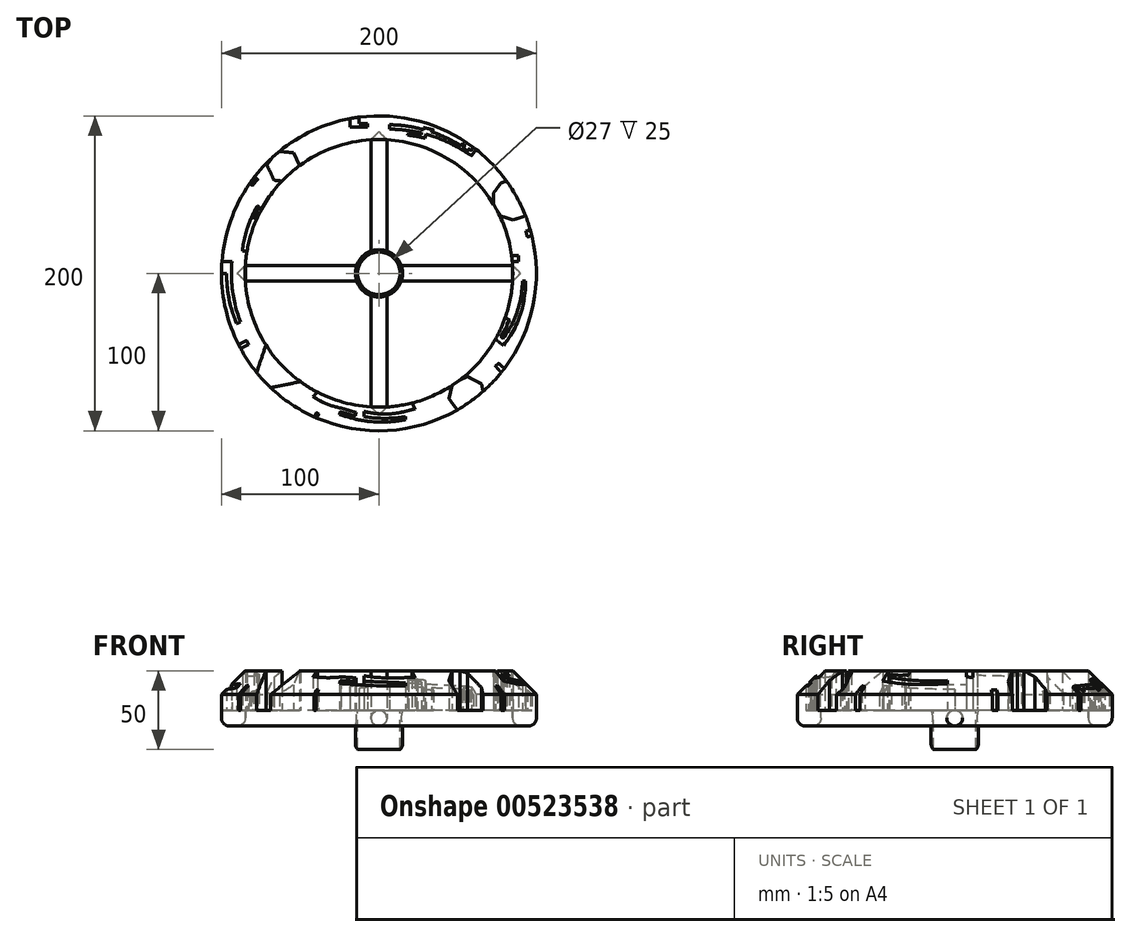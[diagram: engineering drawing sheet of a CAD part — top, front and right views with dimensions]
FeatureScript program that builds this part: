
annotation { "Feature Type Name" : "Feature", "Feature Type Description" : "" }
export const myFeature = defineFeature(function(context is Context, id is Id, definition is map)
    precondition{}
    {
        {
            var Q0;
            Q0=qCreatedBy(makeId("Top.planeOp"),FACE);
            var sketch = newSketch(context, id + "F0", { "sketchPlane" : qUnion([Q0])});
            skArc(sketch, "E0", {"start": v(-5, 14.14) * mm, "mid": v(-10.6, 10.6) * mm, "end": v(-14.14, 5) * mm});
            skCircle(sketch, "E1", {"center": v(0, 0) * mm, "radius": 13.5 * mm});
            skLineSegment(sketch, "E2.left", {"start": v(-5, 84.85) * mm, "end": v(-5, 14.14) * mm});
            skLineSegment(sketch, "E2.right", {"start": v(5, 84.85) * mm, "end": v(5, 14.14) * mm});
            skLineSegment(sketch, "E3.bottom", {"start": v(84.85, 5) * mm, "end": v(14.14, 5) * mm});
            skLineSegment(sketch, "E3.top", {"start": v(84.85, -5) * mm, "end": v(14.14, -5) * mm});
            skArc(sketch, "E4.trimOffspring", {"start": v(14.14, 5) * mm, "mid": v(10.6, 10.6) * mm, "end": v(5, 14.14) * mm});
            skLineSegment(sketch, "E5.MirrorCS", {"start": v(-84.85, 5) * mm, "end": v(-14.14, 5) * mm});
            skLineSegment(sketch, "E6.MirrorCS", {"start": v(-84.85, -5) * mm, "end": v(-14.14, -5) * mm});
            skLineSegment(sketch, "E7.MirrorCS", {"start": v(5, -84.85) * mm, "end": v(5, -14.14) * mm});
            skLineSegment(sketch, "E8.MirrorCS", {"start": v(-5, -84.85) * mm, "end": v(-5, -14.14) * mm});
            skArc(sketch, "E9.trimOffspring", {"start": v(-14.14, -5) * mm, "mid": v(-10.6, -10.6) * mm, "end": v(-5, -14.14) * mm});
            skArc(sketch, "E10.trimOffspring", {"start": v(5, -14.14) * mm, "mid": v(10.6, -10.6) * mm, "end": v(14.14, -5) * mm});
            skCircle(sketch, "E11", {"center": v(0, 0) * mm, "radius": 100 * mm});
            skArc(sketch, "E12", {"start": v(-5, 84.85) * mm, "mid": v(-60.1, 60.1) * mm, "end": v(-84.85, 5) * mm});
            skArc(sketch, "E13.trimOffspring", {"start": v(84.85, 5) * mm, "mid": v(60.1, 60.1) * mm, "end": v(5, 84.85) * mm});
            skArc(sketch, "E14.trimOffspring", {"start": v(5, -84.85) * mm, "mid": v(60.1, -60.1) * mm, "end": v(84.85, -5) * mm});
            skArc(sketch, "E15.trimOffspring", {"start": v(-84.85, -5) * mm, "mid": v(-60.1, -60.1) * mm, "end": v(-5, -84.85) * mm});
            skLineSegment(sketch, "E16", {"start": v(-5, -84.85) * mm, "end": v(5, -84.85) * mm});
            skLineSegment(sketch, "E17", {"start": v(-84.85, 5) * mm, "end": v(-84.85, -5) * mm});
            skLineSegment(sketch, "E18", {"start": v(-5, 84.85) * mm, "end": v(5, 84.85) * mm});
            skLineSegment(sketch, "E19", {"start": v(84.85, 5) * mm, "end": v(84.85, -5) * mm});
            skArc(sketch, "E20", {"start": v(-14.14, 5) * mm, "mid": v(-15, 0) * mm, "end": v(-14.14, -5) * mm});
            skArc(sketch, "E21.MirrorCS", {"start": v(14.14, 5) * mm, "mid": v(15, 0) * mm, "end": v(14.14, -5) * mm});
            skArc(sketch, "E22", {"start": v(5, 14.14) * mm, "mid": v(0, 15) * mm, "end": v(-5, 14.14) * mm});
            skArc(sketch, "E23.MirrorCS", {"start": v(5, -14.14) * mm, "mid": v(0, -15) * mm, "end": v(-5, -14.14) * mm});
            skLineSegment(sketch, "E24", {"start": v(-100, 0) * mm, "end": v(-96.68, 0) * mm});
            skArc(sketch, "E25", {"start": v(-96.68, 0) * mm, "mid": v(-95.19, -16.22) * mm, "end": v(-90.38, -31.79) * mm});
            skLineSegment(sketch, "E26", {"start": v(-90.38, -31.79) * mm, "end": v(-87.85, -30.9) * mm});
            skArc(sketch, "E27", {"start": v(-93.32, 7.4) * mm, "mid": v(-92.88, -12.07) * mm, "end": v(-87.85, -30.9) * mm});
            skLineSegment(sketch, "E28", {"start": v(-93.32, 7.4) * mm, "end": v(-99.73, 7.4) * mm});
            skLineSegment(sketch, "E29", {"start": v(-83.79, 14.3) * mm, "end": v(-86.74, 14.3) * mm});
            skArc(sketch, "E30", {"start": v(-77.16, 42.9) * mm, "mid": v(-83.42, 29.09) * mm, "end": v(-86.74, 14.3) * mm});
            skLineSegment(sketch, "E31", {"start": v(-77.16, 42.9) * mm, "end": v(-76.17, 42.27) * mm});
            skArc(sketch, "E32", {"start": v(-76.17, 42.27) * mm, "mid": v(-77.82, 38.73) * mm, "end": v(-79.37, 35.15) * mm});
            skCircle(sketch, "E33.cCircle", {"center": v(-67.46, -62.6) * mm, "radius": 9.56 * mm, "construction": true});
            skLineSegment(sketch, "E33.0", {"start": v(-71.24, -43.87) * mm, "end": v(-49.35, -68.7) * mm});
            skLineSegment(sketch, "E33.1", {"start": v(-49.35, -68.7) * mm, "end": v(-81.8, -75.24) * mm});
            skLineSegment(sketch, "E33.2", {"start": v(-81.8, -75.24) * mm, "end": v(-71.24, -43.87) * mm});
            skPoint(sketch, "E33.0.midPoint", {"position": v(-60.3, -56.29) * mm});
            skLineSegment(sketch, "E34", {"start": v(-39.13, -75.46) * mm, "end": v(-41.87, -78.2) * mm});
            skArc(sketch, "E35", {"start": v(-41.87, -78.2) * mm, "mid": v(-33.42, -82.83) * mm, "end": v(-24.16, -85.55) * mm});
            skLineSegment(sketch, "E36", {"start": v(-24.16, -85.55) * mm, "end": v(-14.47, -88.4) * mm});
            skLineSegment(sketch, "E37", {"start": v(-14.47, -88.4) * mm, "end": v(-15.12, -90.62) * mm});
            skLineSegment(sketch, "E38", {"start": v(-15.12, -90.62) * mm, "end": v(-24.5, -87.86) * mm});
            skLineSegment(sketch, "E39", {"start": v(-24.5, -87.86) * mm, "end": v(-25, -89.53) * mm});
            skArc(sketch, "E40", {"start": v(-25, -89.53) * mm, "mid": v(-4.24, -94.25) * mm, "end": v(17.01, -92.9) * mm});
            skLineSegment(sketch, "E41", {"start": v(17.01, -92.9) * mm, "end": v(17.01, -91.03) * mm});
            skArc(sketch, "E42", {"start": v(-9.52, -91.03) * mm, "mid": v(3.75, -92.05) * mm, "end": v(17.01, -91.03) * mm});
            skLineSegment(sketch, "E43", {"start": v(-9.52, -91.03) * mm, "end": v(-9.52, -87.66) * mm});
            skArc(sketch, "E44", {"start": v(-9.52, -87.66) * mm, "mid": v(3.6, -89.35) * mm, "end": v(16.74, -87.66) * mm});
            skLineSegment(sketch, "E45", {"start": v(16.74, -87.66) * mm, "end": v(22.99, -86.02) * mm});
            skLineSegment(sketch, "E46", {"start": v(22.99, -86.02) * mm, "end": v(20.92, -82.39) * mm});
            skCircle(sketch, "E47.cCircle", {"center": v(55.83, -77.24) * mm, "radius": 10.55 * mm, "construction": true});
            skLineSegment(sketch, "E47.0", {"start": v(46.85, -69.73) * mm, "end": v(56.1, -65.54) * mm});
            skLineSegment(sketch, "E47.1", {"start": v(56.1, -65.54) * mm, "end": v(65.15, -70.16) * mm});
            skLineSegment(sketch, "E47.2", {"start": v(65.15, -70.16) * mm, "end": v(67.18, -80.12) * mm});
            skLineSegment(sketch, "E47.3", {"start": v(67.18, -80.12) * mm, "end": v(60.66, -87.9) * mm});
            skLineSegment(sketch, "E47.4", {"start": v(60.66, -87.9) * mm, "end": v(50.5, -87.67) * mm});
            skLineSegment(sketch, "E47.5", {"start": v(50.5, -87.67) * mm, "end": v(44.36, -79.58) * mm});
            skLineSegment(sketch, "E47.6", {"start": v(44.36, -79.58) * mm, "end": v(46.85, -69.73) * mm});
            skPoint(sketch, "E47.0.midPoint", {"position": v(51.48, -67.64) * mm});
            skLineSegment(sketch, "E48", {"start": v(77.65, -63) * mm, "end": v(73.98, -58.89) * mm});
            skLineSegment(sketch, "E49", {"start": v(73.98, -58.89) * mm, "end": v(75.97, -57.12) * mm});
            skLineSegment(sketch, "E50", {"start": v(75.97, -57.12) * mm, "end": v(79.75, -60.34) * mm});
            skLineSegment(sketch, "E51", {"start": v(73.99, -41.84) * mm, "end": v(78.99, -45.84) * mm});
            skArc(sketch, "E52", {"start": v(78.99, -45.84) * mm, "mid": v(89.74, -26.58) * mm, "end": v(93.05, -4.77) * mm});
            skLineSegment(sketch, "E53", {"start": v(93.05, -4.77) * mm, "end": v(91.07, -4.77) * mm});
            skArc(sketch, "E54", {"start": v(78.9, -41.47) * mm, "mid": v(87.9, -24.09) * mm, "end": v(91.07, -4.77) * mm});
            skLineSegment(sketch, "E55", {"start": v(78.9, -41.47) * mm, "end": v(77.59, -40.15) * mm});
            skLineSegment(sketch, "E56", {"start": v(77.59, -40.15) * mm, "end": v(81.36, -33.65) * mm});
            skLineSegment(sketch, "E57", {"start": v(81.36, -33.65) * mm, "end": v(81.36, -32.04) * mm});
            skLineSegment(sketch, "E58", {"start": v(81.36, -32.04) * mm, "end": v(82.77, -29.5) * mm});
            skLineSegment(sketch, "E59", {"start": v(82.77, -29.5) * mm, "end": v(80.23, -28.08) * mm});
            skLineSegment(sketch, "E60", {"start": v(84.67, 7.5) * mm, "end": v(88.52, 7.5) * mm});
            skLineSegment(sketch, "E61", {"start": v(88.52, 7.5) * mm, "end": v(88.52, 11.47) * mm});
            skLineSegment(sketch, "E62", {"start": v(88.52, 11.47) * mm, "end": v(84.22, 11.47) * mm});
            skCircle(sketch, "E63.cCircle", {"center": v(85.2, 46.94) * mm, "radius": 12.38 * mm, "construction": true});
            skLineSegment(sketch, "E63.0", {"start": v(77.55, 36.4) * mm, "end": v(72.82, 42.9) * mm});
            skLineSegment(sketch, "E63.1", {"start": v(72.82, 42.9) * mm, "end": v(72.81, 50.95) * mm});
            skLineSegment(sketch, "E63.2", {"start": v(72.81, 50.95) * mm, "end": v(77.54, 57.46) * mm});
            skLineSegment(sketch, "E63.3", {"start": v(77.54, 57.46) * mm, "end": v(85.18, 59.95) * mm});
            skLineSegment(sketch, "E63.4", {"start": v(85.18, 59.95) * mm, "end": v(92.84, 57.47) * mm});
            skLineSegment(sketch, "E63.5", {"start": v(92.84, 57.47) * mm, "end": v(97.57, 50.97) * mm});
            skLineSegment(sketch, "E63.6", {"start": v(97.57, 50.97) * mm, "end": v(97.58, 42.92) * mm});
            skLineSegment(sketch, "E63.7", {"start": v(97.58, 42.92) * mm, "end": v(92.85, 36.41) * mm});
            skLineSegment(sketch, "E63.8", {"start": v(92.85, 36.41) * mm, "end": v(85.2, 33.92) * mm});
            skLineSegment(sketch, "E63.9", {"start": v(85.2, 33.92) * mm, "end": v(77.55, 36.4) * mm});
            skPoint(sketch, "E63.0.midPoint", {"position": v(75.19, 39.65) * mm});
            skLineSegment(sketch, "E64", {"start": v(96.13, 27.54) * mm, "end": v(93.26, 26.73) * mm});
            skLineSegment(sketch, "E65", {"start": v(93.26, 26.73) * mm, "end": v(94.27, 23.14) * mm});
            skLineSegment(sketch, "E66", {"start": v(94.27, 23.14) * mm, "end": v(97.1, 23.93) * mm});
            skLineSegment(sketch, "E67", {"start": v(-39.8, -91.74) * mm, "end": v(-38.3, -89.3) * mm});
            skLineSegment(sketch, "E68", {"start": v(-38.3, -89.3) * mm, "end": v(-39.65, -88.48) * mm});
            skLineSegment(sketch, "E69", {"start": v(-39.65, -88.48) * mm, "end": v(-41.26, -91.1) * mm});
            skLineSegment(sketch, "E70", {"start": v(-89.13, -45.34) * mm, "end": v(-84.06, -42.72) * mm});
            skLineSegment(sketch, "E71", {"start": v(-84.06, -42.72) * mm, "end": v(-82.82, -45.13) * mm});
            skLineSegment(sketch, "E72", {"start": v(-82.82, -45.13) * mm, "end": v(-87.87, -47.74) * mm});
            skCircle(sketch, "E73.cCircle", {"center": v(-60.49, 67.89) * mm, "radius": 9.28 * mm, "construction": true});
            skLineSegment(sketch, "E73.0", {"start": v(-71.15, 68.96) * mm, "end": v(-64.89, 77.65) * mm});
            skLineSegment(sketch, "E73.1", {"start": v(-64.89, 77.65) * mm, "end": v(-54.23, 76.58) * mm});
            skLineSegment(sketch, "E73.2", {"start": v(-54.23, 76.58) * mm, "end": v(-49.82, 66.81) * mm});
            skLineSegment(sketch, "E73.3", {"start": v(-49.82, 66.81) * mm, "end": v(-56.08, 58.12) * mm});
            skLineSegment(sketch, "E73.4", {"start": v(-56.08, 58.12) * mm, "end": v(-66.74, 59.19) * mm});
            skLineSegment(sketch, "E73.5", {"start": v(-66.74, 59.19) * mm, "end": v(-71.15, 68.96) * mm});
            skPoint(sketch, "E73.0.midPoint", {"position": v(-68.02, 73.3) * mm});
            skLineSegment(sketch, "E74", {"start": v(-79.37, 35.15) * mm, "end": v(-77.84, 34.16) * mm});
            skLineSegment(sketch, "E75", {"start": v(-82.17, 56.99) * mm, "end": v(-80.14, 55.86) * mm});
            skLineSegment(sketch, "E76", {"start": v(-80.14, 55.86) * mm, "end": v(-78.62, 57.77) * mm});
            skLineSegment(sketch, "E77", {"start": v(-78.62, 57.77) * mm, "end": v(-77, 59.62) * mm});
            skLineSegment(sketch, "E78", {"start": v(-77, 59.62) * mm, "end": v(-77.79, 60.31) * mm});
            skLineSegment(sketch, "E79", {"start": v(-77.79, 60.31) * mm, "end": v(-79.63, 58.22) * mm});
            skLineSegment(sketch, "E80", {"start": v(-79.63, 58.22) * mm, "end": v(-81.06, 58.56) * mm});
            skLineSegment(sketch, "E81", {"start": v(61.81, 78.6) * mm, "end": v(58.84, 74.8) * mm});
            skLineSegment(sketch, "E82", {"start": v(58.84, 74.8) * mm, "end": v(51.74, 79.02) * mm});
            skArc(sketch, "E83", {"start": v(51.74, 79.02) * mm, "mid": v(41.1, 84.42) * mm, "end": v(29.84, 88.35) * mm});
            skLineSegment(sketch, "E84", {"start": v(6.7, 91.56) * mm, "end": v(6.7, 94.36) * mm});
            skArc(sketch, "E85", {"start": v(28.45, 91.11) * mm, "mid": v(17.7, 93.58) * mm, "end": v(6.7, 94.36) * mm});
            skLineSegment(sketch, "E86", {"start": v(28.45, 91.11) * mm, "end": v(28.45, 92.57) * mm});
            skLineSegment(sketch, "E87", {"start": v(28.45, 92.57) * mm, "end": v(34.73, 91.11) * mm});
            skLineSegment(sketch, "E88", {"start": v(34.73, 91.11) * mm, "end": v(33.38, 89.88) * mm});
            skArc(sketch, "E89", {"start": v(52, 81.13) * mm, "mid": v(42.94, 86.04) * mm, "end": v(33.38, 89.88) * mm});
            skLineSegment(sketch, "E90", {"start": v(52, 81.13) * mm, "end": v(53, 82.36) * mm});
            skLineSegment(sketch, "E91", {"start": v(53, 82.36) * mm, "end": v(54.52, 81.13) * mm});
            skLineSegment(sketch, "E92", {"start": v(54.52, 81.13) * mm, "end": v(53.54, 79.94) * mm});
            skLineSegment(sketch, "E93", {"start": v(53.54, 79.94) * mm, "end": v(56.18, 77.78) * mm});
            skLineSegment(sketch, "E94", {"start": v(56.18, 77.78) * mm, "end": v(57.2, 79.04) * mm});
            skLineSegment(sketch, "E95", {"start": v(57.2, 79.04) * mm, "end": v(58.37, 78.08) * mm});
            skLineSegment(sketch, "E96", {"start": v(58.37, 78.08) * mm, "end": v(59.97, 80.02) * mm});
            skLineSegment(sketch, "E97", {"start": v(24.01, 86.97) * mm, "end": v(29.33, 85.87) * mm});
            skLineSegment(sketch, "E98", {"start": v(29.33, 85.87) * mm, "end": v(29.84, 88.35) * mm});
            skArc(sketch, "E99.trimOffspring", {"start": v(24.56, 89.64) * mm, "mid": v(15.68, 91.05) * mm, "end": v(6.7, 91.56) * mm});
            skLineSegment(sketch, "E100", {"start": v(24.01, 86.97) * mm, "end": v(18.03, 87.87) * mm});
            skLineSegment(sketch, "E101", {"start": v(18.03, 87.87) * mm, "end": v(18.88, 88.9) * mm});
            skLineSegment(sketch, "E102", {"start": v(27.09, 88.05) * mm, "end": v(27.09, 89.47) * mm});
            skLineSegment(sketch, "E103", {"start": v(27.09, 89.47) * mm, "end": v(24.56, 89.64) * mm});
            skArc(sketch, "E104", {"start": v(27.09, 88.05) * mm, "mid": v(23, 88.6) * mm, "end": v(18.88, 88.9) * mm});
            skLineSegment(sketch, "E105", {"start": v(-12.67, 99.2) * mm, "end": v(-12.67, 95.26) * mm});
            skLineSegment(sketch, "E106", {"start": v(-12.67, 95.26) * mm, "end": v(-7.13, 95.26) * mm});
            skLineSegment(sketch, "E107", {"start": v(-7.13, 95.26) * mm, "end": v(-7.13, 93) * mm});
            skLineSegment(sketch, "E108", {"start": v(-7.13, 93) * mm, "end": v(-13.92, 93) * mm});
            skLineSegment(sketch, "E109", {"start": v(-13.92, 93) * mm, "end": v(-18.45, 93) * mm});
            skLineSegment(sketch, "E110", {"start": v(-18.45, 93) * mm, "end": v(-18.45, 98.28) * mm});
            skArc(sketch, "E111", {"start": v(-20.15, 86.4) * mm, "mid": v(-34.73, 82.8) * mm, "end": v(-47.5, 74.9) * mm});
            skLineSegment(sketch, "E112", {"start": v(-20.15, 86.4) * mm, "end": v(-20.15, 88.63) * mm});
            skLineSegment(sketch, "E113", {"start": v(-47.5, 74.9) * mm, "end": v(-47.5, 79.2) * mm});
            skArc(sketch, "E114", {"start": v(-20.15, 88.63) * mm, "mid": v(-34.22, 85.34) * mm, "end": v(-47.3, 79.2) * mm});
            skSolve(sketch);
        }
        {
            var Q0;
            Q0=qCreatedBy(makeId("Top.planeOp"),FACE);
            var sketch = newSketch(context, id + "F1", { "sketchPlane" : qUnion([Q0])});
            skCircle(sketch, "E115", {"center": v(0, 0) * mm, "radius": 13.5 * mm});
            skCircle(sketch, "E116", {"center": v(0, 0) * mm, "radius": 15 * mm});
            skCircle(sketch, "E117", {"center": v(0, 0) * mm, "radius": 100 * mm});
            skCircle(sketch, "E118", {"center": v(0, 0) * mm, "radius": 85 * mm});
            skLineSegment(sketch, "E119", {"start": v(-14.14, 5) * mm, "end": v(-84.85, 5) * mm});
            skLineSegment(sketch, "E120", {"start": v(-14.14, -5) * mm, "end": v(-84.85, -5) * mm});
            skLineSegment(sketch, "E121", {"start": v(-5, 84.85) * mm, "end": v(-5, 14.14) * mm});
            skLineSegment(sketch, "E122", {"start": v(5, 14.14) * mm, "end": v(5, 84.85) * mm});
            skLineSegment(sketch, "E123.MirrorCS", {"start": v(14.14, 5) * mm, "end": v(84.85, 5) * mm});
            skLineSegment(sketch, "E124.MirrorCS", {"start": v(14.14, -5) * mm, "end": v(84.85, -5) * mm});
            skLineSegment(sketch, "E125.MirrorCS", {"start": v(-5, -84.85) * mm, "end": v(-5, -14.14) * mm});
            skLineSegment(sketch, "E126.MirrorCS", {"start": v(5, -14.14) * mm, "end": v(5, -84.85) * mm});
            skSolve(sketch);
        }
        {
            var Q0;
            Q0=qCreatedBy(makeId("Top.planeOp"),FACE);
            var sketch = newSketch(context, id + "F2", { "sketchPlane" : qUnion([Q0])});
            skCircle(sketch, "E127", {"center": v(0, 0) * mm, "radius": 13.5 * mm});
            skCircle(sketch, "E128", {"center": v(0, 0) * mm, "radius": 15 * mm});
            skSolve(sketch);
        }
        {
            var Q0;
            {var subQ7=sQuery(id+"F0.wireOp",EDGE,"E34");Q0=makeQuery(id+"F0.imprint","IMPRINT",FACE,{"disambiguationData":[TD([[makeQuery(id+"F0.imprint","IMPRINT",EDGE,{"derivedFrom":subQ7}),-1.0]])]});}
            var Q1;
            {var subQ19=sQuery(id+"F0.wireOp",EDGE,"E17");Q1=makeQuery(id+"F0.imprint","IMPRINT",FACE,{"disambiguationData":[TD([[makeQuery(id+"F0.imprint","IMPRINT",EDGE,{"derivedFrom":subQ19}),-1.0]])]});}
            var Q2;
            {var subQ1=sQuery(id+"F0.wireOp",EDGE,"E18");Q2=makeQuery(id+"F0.imprint","IMPRINT",FACE,{"disambiguationData":[TD([[makeQuery(id+"F0.imprint","IMPRINT",EDGE,{"derivedFrom":subQ1}),1.0]])]});}
            var Q3;
            {var subQ6=sQuery(id+"F0.wireOp",EDGE,"E19");Q3=makeQuery(id+"F0.imprint","IMPRINT",FACE,{"disambiguationData":[TD([[makeQuery(id+"F0.imprint","IMPRINT",EDGE,{"derivedFrom":subQ6}),1.0]])]});}
            extrude(context, id + "F3", {"entities" : qUnion([Q0, Q1, Q2, Q3]), "depth" : 25 * mm, "offsetDistance" : 25 * mm});
        }
        {
            var Q0;
            Q0=makeQuery(id+"F1.imprint","IMPRINT",FACE,{"disambiguationData":[TD([[makeQuery(id+"F1.imprint","IMPRINT",EDGE,{"derivedFrom":sQuery(id+"F1.wireOp",EDGE,"E117")}),1.0]])]});
            var Q1;
            {var subQ0=sQuery(id+"F1.wireOp",EDGE,"E121");Q1=makeQuery(id+"F1.imprint","IMPRINT",FACE,{"disambiguationData":[TD([[makeQuery(id+"F1.imprint","IMPRINT",EDGE,{"derivedFrom":subQ0}),1.0]])]});}
            var Q2;
            {var subQ0=sQuery(id+"F1.wireOp",EDGE,"E119");Q2=makeQuery(id+"F1.imprint","IMPRINT",FACE,{"disambiguationData":[TD([[makeQuery(id+"F1.imprint","IMPRINT",EDGE,{"derivedFrom":subQ0}),1.0]])]});}
            var Q3;
            {var subQ0=sQuery(id+"F1.wireOp",EDGE,"E123.MirrorCS");Q3=makeQuery(id+"F1.imprint","IMPRINT",FACE,{"disambiguationData":[TD([[makeQuery(id+"F1.imprint","IMPRINT",EDGE,{"derivedFrom":subQ0}),-1.0]])]});}
            var Q4;
            {var subQ0=sQuery(id+"F1.wireOp",EDGE,"E125.MirrorCS");Q4=makeQuery(id+"F1.imprint","IMPRINT",FACE,{"disambiguationData":[TD([[makeQuery(id+"F1.imprint","IMPRINT",EDGE,{"derivedFrom":subQ0}),-1.0]])]});}
            var Q5;
            Q5=makeQuery(id+"F1.imprint","IMPRINT",FACE,{"disambiguationData":[TD([[makeQuery(id+"F1.imprint","IMPRINT",EDGE,{"derivedFrom":sQuery(id+"F1.wireOp",EDGE,"E115")}),-1.0]])]});
            extrude(context, id + "F4", {"entities" : qUnion([Q0, Q1, Q2, Q3, Q4, Q5]), "operationType" : NewBodyOperationType.ADD, "oppositeDirection" : true, "depth" : 10 * mm, "offsetDistance" : 25 * mm});
        }
        {
            var Q0;
            Q0=makeQuery(id+"F4.opExtrude","CAP_EDGE",EDGE,{"disambiguationData":[OSD([sQuery(id+"F1.wireOp",EDGE,"E124.MirrorCS")])],"isStart":false});
            var Q1;
            Q1=makeQuery(id+"F4.opExtrude","CAP_EDGE",EDGE,{"disambiguationData":[OSD([sQuery(id+"F1.wireOp",EDGE,"E123.MirrorCS")])],"isStart":false});
            var Q2;
            Q2=makeQuery(id+"F4.opExtrude","CAP_EDGE",EDGE,{"disambiguationData":[OSD([sQuery(id+"F1.wireOp",EDGE,"E124.MirrorCS")])],"isStart":true});
            var Q3;
            Q3=makeQuery(id+"F4.opExtrude","CAP_EDGE",EDGE,{"disambiguationData":[OSD([sQuery(id+"F1.wireOp",EDGE,"E123.MirrorCS")])],"isStart":true});
            var Q4;
            Q4=makeQuery(id+"F4.opExtrude","CAP_EDGE",EDGE,{"disambiguationData":[OSD([sQuery(id+"F1.wireOp",EDGE,"E126.MirrorCS")])],"isStart":false});
            var Q5;
            Q5=makeQuery(id+"F4.opExtrude","CAP_EDGE",EDGE,{"disambiguationData":[OSD([sQuery(id+"F1.wireOp",EDGE,"E125.MirrorCS")])],"isStart":false});
            var Q6;
            Q6=makeQuery(id+"F4.opExtrude","CAP_EDGE",EDGE,{"disambiguationData":[OSD([sQuery(id+"F1.wireOp",EDGE,"E125.MirrorCS")])],"isStart":true});
            var Q7;
            Q7=makeQuery(id+"F4.opExtrude","CAP_EDGE",EDGE,{"disambiguationData":[OSD([sQuery(id+"F1.wireOp",EDGE,"E126.MirrorCS")])],"isStart":true});
            var Q8;
            Q8=makeQuery(id+"F4.opExtrude","CAP_EDGE",EDGE,{"disambiguationData":[OSD([sQuery(id+"F1.wireOp",EDGE,"E120")])],"isStart":true});
            var Q9;
            Q9=makeQuery(id+"F4.opExtrude","CAP_EDGE",EDGE,{"disambiguationData":[OSD([sQuery(id+"F1.wireOp",EDGE,"E120")])],"isStart":false});
            var Q10;
            Q10=makeQuery(id+"F4.opExtrude","CAP_EDGE",EDGE,{"disambiguationData":[OSD([sQuery(id+"F1.wireOp",EDGE,"E119")])],"isStart":false});
            var Q11;
            Q11=makeQuery(id+"F4.opExtrude","CAP_EDGE",EDGE,{"disambiguationData":[OSD([sQuery(id+"F1.wireOp",EDGE,"E119")])],"isStart":true});
            var Q12;
            Q12=makeQuery(id+"F4.opExtrude","CAP_EDGE",EDGE,{"disambiguationData":[OSD([sQuery(id+"F1.wireOp",EDGE,"E122")])],"isStart":false});
            var Q13;
            Q13=makeQuery(id+"F4.opExtrude","CAP_EDGE",EDGE,{"disambiguationData":[OSD([sQuery(id+"F1.wireOp",EDGE,"E122")])],"isStart":true});
            var Q14;
            Q14=makeQuery(id+"F4.opExtrude","CAP_EDGE",EDGE,{"disambiguationData":[OSD([sQuery(id+"F1.wireOp",EDGE,"E121")])],"isStart":true});
            var Q15;
            Q15=makeQuery(id+"F4.opExtrude","CAP_EDGE",EDGE,{"disambiguationData":[OSD([sQuery(id+"F1.wireOp",EDGE,"E121")])],"isStart":false});
            var Q16;
            {var subQ0=sQuery(id+"F1.wireOp",EDGE,"E118");Q16=makeQuery(id+"F4.opExtrude","CAP_EDGE",EDGE,{"disambiguationData":[OSD([subQ0]),TDD([makeQuery(id+"F1.imprint","IMPRINT",EDGE,{"disambiguationData":[TD([[makeQuery(id+"F1.imprint","INTERSECT",VERTEX,{"derivedFrom":[subQ0,sQuery(id+"F1.wireOp",EDGE,"E119")]}),1.0]])],"derivedFrom":subQ0})])],"isStart":false});}
            var Q17;
            {var subQ0=sQuery(id+"F1.wireOp",EDGE,"E118");Q17=makeQuery(id+"F4.opExtrude","CAP_EDGE",EDGE,{"disambiguationData":[OSD([subQ0]),TDD([makeQuery(id+"F1.imprint","IMPRINT",EDGE,{"disambiguationData":[TD([[makeQuery(id+"F1.imprint","INTERSECT",VERTEX,{"derivedFrom":[subQ0,sQuery(id+"F1.wireOp",EDGE,"E122")]}),1.0]])],"derivedFrom":subQ0})])],"isStart":false});}
            var Q18;
            Q18=makeQuery(id+"F4.opExtrude","CAP_EDGE",EDGE,{"disambiguationData":[OSD([sQuery(id+"F1.wireOp",EDGE,"E117")])],"isStart":false});
            var Q19;
            {var subQ0=sQuery(id+"F1.wireOp",EDGE,"E118");Q19=makeQuery(id+"F4.opExtrude","CAP_EDGE",EDGE,{"disambiguationData":[OSD([subQ0]),TDD([makeQuery(id+"F1.imprint","IMPRINT",EDGE,{"disambiguationData":[TD([[makeQuery(id+"F1.imprint","INTERSECT",VERTEX,{"derivedFrom":[subQ0,sQuery(id+"F1.wireOp",EDGE,"E124.MirrorCS")]}),1.0]])],"derivedFrom":subQ0})])],"isStart":false});}
            var Q20;
            {var subQ0=sQuery(id+"F1.wireOp",EDGE,"E118");Q20=makeQuery(id+"F4.opExtrude","CAP_EDGE",EDGE,{"disambiguationData":[OSD([subQ0]),TDD([makeQuery(id+"F1.imprint","IMPRINT",EDGE,{"disambiguationData":[TD([[makeQuery(id+"F1.imprint","INTERSECT",VERTEX,{"derivedFrom":[subQ0,sQuery(id+"F1.wireOp",EDGE,"E120")]}),-1.0]])],"derivedFrom":subQ0})])],"isStart":false});}
            var Q21;
            {var subQ0=sQuery(id+"F1.wireOp",EDGE,"E116");Q21=makeQuery(id+"F4.opExtrude","CAP_EDGE",EDGE,{"disambiguationData":[OSD([subQ0]),TDD([makeQuery(id+"F1.imprint","IMPRINT",EDGE,{"disambiguationData":[TD([[makeQuery(id+"F1.imprint","INTERSECT",VERTEX,{"derivedFrom":[subQ0,sQuery(id+"F1.wireOp",EDGE,"E120")]}),-1.0]])],"derivedFrom":subQ0})])],"isStart":true});}
            var Q22;
            {var subQ0=sQuery(id+"F1.wireOp",EDGE,"E116");Q22=makeQuery(id+"F4.opExtrude","CAP_EDGE",EDGE,{"disambiguationData":[OSD([subQ0]),TDD([makeQuery(id+"F1.imprint","IMPRINT",EDGE,{"disambiguationData":[TD([[makeQuery(id+"F1.imprint","INTERSECT",VERTEX,{"derivedFrom":[subQ0,sQuery(id+"F1.wireOp",EDGE,"E124.MirrorCS")]}),1.0]])],"derivedFrom":subQ0})])],"isStart":true});}
            var Q23;
            {var subQ0=sQuery(id+"F1.wireOp",EDGE,"E116");Q23=makeQuery(id+"F4.opExtrude","CAP_EDGE",EDGE,{"disambiguationData":[OSD([subQ0]),TDD([makeQuery(id+"F1.imprint","IMPRINT",EDGE,{"disambiguationData":[TD([[makeQuery(id+"F1.imprint","INTERSECT",VERTEX,{"derivedFrom":[subQ0,sQuery(id+"F1.wireOp",EDGE,"E122")]}),1.0]])],"derivedFrom":subQ0})])],"isStart":true});}
            var Q24;
            {var subQ0=sQuery(id+"F1.wireOp",EDGE,"E116");Q24=makeQuery(id+"F4.opExtrude","CAP_EDGE",EDGE,{"disambiguationData":[OSD([subQ0]),TDD([makeQuery(id+"F1.imprint","IMPRINT",EDGE,{"disambiguationData":[TD([[makeQuery(id+"F1.imprint","INTERSECT",VERTEX,{"derivedFrom":[subQ0,sQuery(id+"F1.wireOp",EDGE,"E119")]}),1.0]])],"derivedFrom":subQ0})])],"isStart":true});}
            fillet(context, id + "F5", {"entities" : qUnion([Q0, Q1, Q2, Q3, Q4, Q5, Q6, Q7, Q8, Q9, Q10, Q11, Q12, Q13, Q14, Q15, Q16, Q17, Q18, Q19, Q20, Q21, Q22, Q23, Q24]), "radius" : 5 * mm, "tangentPropagation" : true, "allowEdgeOverflow" : false});
        }
        {
            var Q0;
            {var subQ0=sQuery(id+"F0.wireOp",EDGE,"E11");Q0=makeQuery(id+"F3.opExtrude","CAP_EDGE",EDGE,{"disambiguationData":[OSD([subQ0]),TDD([makeQuery(id+"F0.imprint","IMPRINT",EDGE,{"disambiguationData":[TD([[makeQuery(id+"F0.imprint","INTERSECT",VERTEX,{"derivedFrom":[subQ0,sQuery(id+"F0.wireOp",EDGE,"E67")]}),-1.0]])],"derivedFrom":subQ0})])],"isStart":false});}
            var Q1;
            {var subQ0=sQuery(id+"F0.wireOp",EDGE,"E11");Q1=makeQuery(id+"F3.opExtrude","CAP_EDGE",EDGE,{"disambiguationData":[OSD([subQ0]),TDD([makeQuery(id+"F0.imprint","IMPRINT",EDGE,{"disambiguationData":[TD([[makeQuery(id+"F0.imprint","INTERSECT",VERTEX,{"derivedFrom":[subQ0,sQuery(id+"F0.wireOp",EDGE,"E50")]}),-1.0]])],"derivedFrom":subQ0})])],"isStart":false});}
            var Q2;
            {var subQ0=sQuery(id+"F0.wireOp",EDGE,"E11");Q2=makeQuery(id+"F3.opExtrude","CAP_EDGE",EDGE,{"disambiguationData":[OSD([subQ0]),TDD([makeQuery(id+"F0.imprint","IMPRINT",EDGE,{"disambiguationData":[TD([[makeQuery(id+"F0.imprint","INTERSECT",VERTEX,{"derivedFrom":[subQ0,sQuery(id+"F0.wireOp",EDGE,"E81")]}),1.0]])],"derivedFrom":subQ0})])],"isStart":false});}
            var Q3;
            {var subQ0=sQuery(id+"F0.wireOp",EDGE,"E11");Q3=makeQuery(id+"F3.opExtrude","CAP_EDGE",EDGE,{"disambiguationData":[OSD([subQ0]),TDD([makeQuery(id+"F0.imprint","IMPRINT",EDGE,{"disambiguationData":[TD([[makeQuery(id+"F0.imprint","INTERSECT",VERTEX,{"derivedFrom":[subQ0,sQuery(id+"F0.wireOp",EDGE,"E24")]}),-1.0]])],"derivedFrom":subQ0})])],"isStart":false});}
            chamfer(context, id + "F6", {"entities" : qUnion([Q0, Q1, Q2, Q3]), "width" : 15 * mm, "tangentPropagation" : true});
        }
        {
            var Q0;
            Q0 = qSketchRegion(id + "F2", true);
            extrude(context, id + "F7", {"entities" : qUnion([Q0]), "operationType" : NewBodyOperationType.ADD, "oppositeDirection" : true, "depth" : 25 * mm, "offsetDistance" : 25 * mm});
        }
        {
            var Q0;
            Q0=makeQuery(id+"F7.opExtrude","CAP_EDGE",EDGE,{"disambiguationData":[OSD([sQuery(id+"F2.wireOp",EDGE,"E128")])],"isStart":false});
            fillet(context, id + "F8", {"entities" : qUnion([Q0]), "radius" : 5 * mm, "tangentPropagation" : true, "allowEdgeOverflow" : false});
        }
    });
